# Revit family: Touch_panel-Z41_PRO-A_-S_-W_-AP_-SP_-WP
name_source: partatom
category: Equipos especializados
revit_build: Autodesk Revit 2018 (Build: 20170927_1515(x64)
units: mm (PartAtom-declared; Revit-internal decimal feet)

## family parameters
Anfitrión = Cara
Compartido = No
Corte con vacíos al cargar = No
Cota de conector redondo = Diámetro de uso
Punto de cálculo de habitación = No
Tipo de pieza = Normal

## types (12) — shared parameters
Analog/digital inputs = 2
BCU = Integrated KNX BCU
Complementary characteristics = Class B
Configurable pages = 12
Connection type = Typical TP1 bus connector for rigid cable 0.80 mm diameter
Degree of protection = IP20, clean environment
Depth = 12 mm  [stored 0.0393701 ft]
Depth_total = 30 mm  [stored 0.0984252 ft]
Descripción = 4.1'' Color Capacitive Touch Panel with IP Connection
Device action type = Type 1
Direct control (indicator functions) = 96
Display Type = 16 million colors LCD display
Electrical stress period = Long
Elevación por defecto = 1219 mm
Ethernet connector = RJ45 connector with 4 poles
External power supply = 12-29 VDC. Maximum consumption: 160mA (12VDC), 76mA (24VDC), 64mA (29VDC)
External power supply connection = Pluggable screw terminal block
Fabricante = Zennio Avance y Tecnología, S.L.
Fit = Magnetic fit
Height = 123 mm
Internal clock = Real Time Clock (RTC) with watch battery
Maximum consumption 24 VDC = 10mA, 240mW
Maximum consumption 29 VDC typical = 6mA, 174mW
Operating humidity = 5 to 95% RH (no condensation)
Operating temperature = 0ºC to +45ºC
Operation type = Continuous operation
Orientation = Portrait or landscape
PCB CTI index = 175 V
Product Page URL = http://www.zennio.com
Protection class = III
Storage humidity = 5 to 95% RH (no condensation)
Storage temperature = -20ºC to +60ºC
Temperature sensor (measuring range) = -10ºC to +50ºC
Temperature sensor (resolution) = 0.1ºC
Thermostats = 2
Touch screen material = Touch screen
URL = http://www.zennio.com
USB connector = Mini USB Type A connector. Version 2.0
Voltage range (KNX supply) = 21...31VDC
Voltage typical (KNX supply) = 29VDC SELV
Width = 90 mm

## per-type parameters (varying)
| type | Constraints | Constraints2 | Constraints3 | Flush | Frame material | Housing material | Surface | Weight |
| ZVI-Z41PRO-AP_surface | 2 | 1 | 1 | No | Polycarbonate frame - Anthracite | PC/ABS FR V0 halogen free - Anthracite | Sí | 226g including battery 1g |
| ZVI-Z41PRO-SP_surface | 2 | 2 | 1 | No | Polycarbonate frame - Silver | PC/ABS FR V0 halogen free - Silver | Sí | 226g including battery 1g |
| ZVI-Z41PRO-WP_surface | 2 | 3 | 1 | No | Polycarbonate frame - White | PC/ABS FR V0 halogen free - White | Sí | 226g including battery 1g |
| ZVI-Z41PRO-AP_flush | 2 | 1 | 2 | Sí | Polycarbonate frame - Anthracite | PC/ABS FR V0 halogen free - Anthracite | No | 226g including battery 1g |
| ZVI-Z41PRO-SP_flush | 2 | 2 | 2 | Sí | Polycarbonate frame - Silver | PC/ABS FR V0 halogen free - Silver | No | 226g including battery 1g |
| ZVI-Z41PRO-WP_flush | 2 | 3 | 2 | Sí | Polycarbonate frame - White | PC/ABS FR V0 halogen free - White | No | 226g including battery 1g |
| ZVI-Z41PRO-A_surface | 1 | 1 | 1 | No | Aluminium frame | PC/ABS FR V0 halogen free - Anthracite | Sí | 237g |
| ZVI-Z41PRO-A_flush | 1 | 1 | 2 | Sí | Aluminium frame | PC/ABS FR V0 halogen free - Anthracite | No | 237g |
| ZVI-Z41PRO-S_surface | 1 | 2 | 1 | No | Aluminium frame | PC/ABS FR V0 halogen free - Silver | Sí | 237g |
| ZVI-Z41PRO-S_flush | 1 | 2 | 2 | Sí | Aluminium frame | PC/ABS FR V0 halogen free - Silver | No | 237g |
| ZVI-Z41PRO-W_surface | 1 | 3 | 1 | No | Aluminium frame | PC/ABS FR V0 halogen free - White | Sí | 237g |
| ZVI-Z41PRO-W_flush | 1 | 3 | 2 | Sí | Aluminium frame | PC/ABS FR V0 halogen free - White | No | 237g |

note: column(s) folded — value = type name in every type: Modelo

note: [stored X ft] marks values corroborated as IEEE doubles in the binary element streams (Revit-internal decimal feet)

## geometry (parser evidence)
native form markers: Sweep x2
no freeform markers — native parametric forms only
